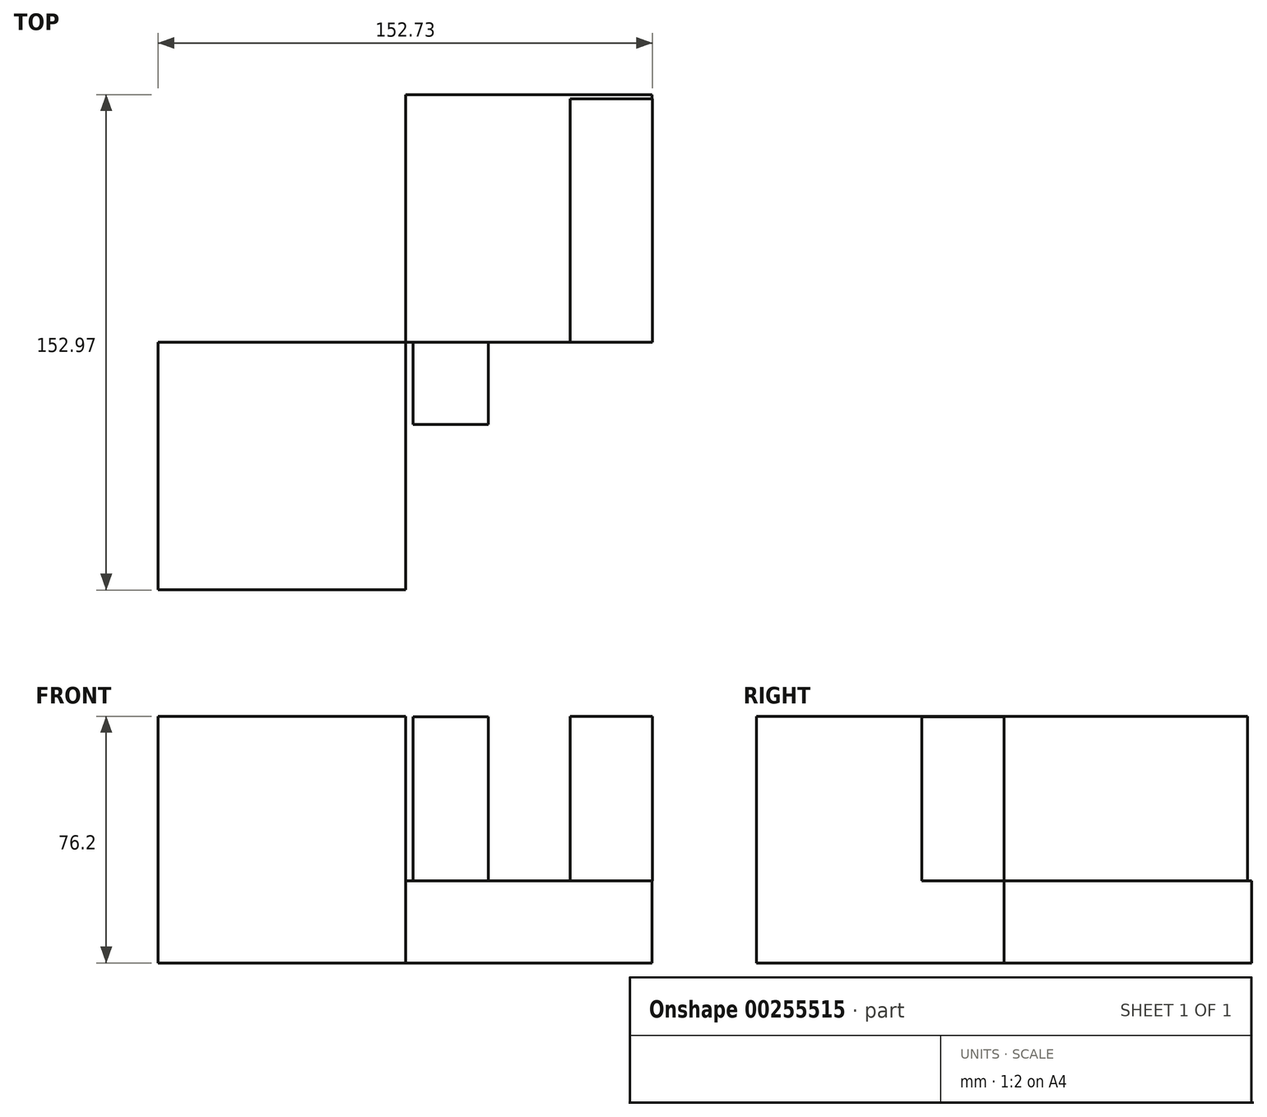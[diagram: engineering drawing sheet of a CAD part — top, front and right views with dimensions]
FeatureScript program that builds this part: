
annotation { "Feature Type Name" : "Feature", "Feature Type Description" : "" }
export const myFeature = defineFeature(function(context is Context, id is Id, definition is map)
    precondition{}
    {
        {
            var Q0;
            Q0=qCreatedBy(makeId("Top.planeOp"),FACE);
            var sketch = newSketch(context, id + "F0", { "sketchPlane" : qUnion([Q0])});
            skLineSegment(sketch, "E0.bottom", {"start": v(76, 76.48) * mm, "end": v(0, 76.48) * mm});
            skLineSegment(sketch, "E0.top", {"start": v(76, 0) * mm, "end": v(0, 0) * mm});
            skLineSegment(sketch, "E0.left", {"start": v(76, 76.48) * mm, "end": v(76, 0) * mm});
            skLineSegment(sketch, "E0.right", {"start": v(0, 76.48) * mm, "end": v(0, 0) * mm});
            skSolve(sketch);
        }
        {
            var Q0;
            Q0 = qSketchRegion(id + "F0", true);
            extrude(context, id + "F1", {"entities" : qUnion([Q0]), "depth" : 25.4 * mm});
        }
        {
            var Q0;
            Q0=qCreatedBy(makeId("Front.planeOp"),FACE);
            var sketch = newSketch(context, id + "F2", { "sketchPlane" : qUnion([Q0])});
            skLineSegment(sketch, "E1.bottom", {"start": v(2.7, 25.84) * mm, "end": v(76.24, 25.84) * mm});
            skLineSegment(sketch, "E1.top", {"start": v(2.7, 75.9) * mm, "end": v(76.24, 75.9) * mm});
            skLineSegment(sketch, "E1.left", {"start": v(2.7, 25.84) * mm, "end": v(2.7, 75.9) * mm});
            skLineSegment(sketch, "E1.right", {"start": v(76.24, 25.84) * mm, "end": v(76.24, 75.9) * mm});
            skSolve(sketch);
        }
        {
            var Q0;
            Q0 = qSketchRegion(id + "F2", true);
            extrude(context, id + "F3", {"entities" : qUnion([Q0]), "depth" : 25.4 * mm});
        }
        {
            var Q0;
            Q0=qCreatedBy(makeId("Right.planeOp"),FACE);
            var sketch = newSketch(context, id + "F4", { "sketchPlane" : qUnion([Q0])});
            skLineSegment(sketch, "E2.bottom", {"start": v(0, 76.17) * mm, "end": v(75.27, 76.17) * mm});
            skLineSegment(sketch, "E2.top", {"start": v(0, 25.38) * mm, "end": v(75.27, 25.38) * mm});
            skLineSegment(sketch, "E2.left", {"start": v(0, 76.17) * mm, "end": v(0, 25.38) * mm});
            skLineSegment(sketch, "E2.right", {"start": v(75.27, 76.17) * mm, "end": v(75.27, 25.38) * mm});
            skSolve(sketch);
        }
        {
            var Q0;
            Q0 = qSketchRegion(id + "F4", true);
            extrude(context, id + "F5", {"entities" : qUnion([Q0]), "depth" : 25.4 * mm});
        }
        {
            var Q0;
            Q0=makeQuery(id+"F5.opExtrude","CAP_FACE",FACE,{"disambiguationData":[OSD([sQuery(id+"F4.wireOp",EDGE,"E2.bottom"),sQuery(id+"F4.wireOp",EDGE,"E2.top"),sQuery(id+"F4.wireOp",EDGE,"E2.left"),sQuery(id+"F4.wireOp",EDGE,"E2.right")])],"isStart":false});
            var sketch = newSketch(context, id + "F6", { "sketchPlane" : qUnion([Q0])});
            skLineSegment(sketch, "E3.bottom", {"start": v(75.27, 76.17) * mm, "end": v(0, 76.17) * mm});
            skLineSegment(sketch, "E3.top", {"start": v(75.27, 25.38) * mm, "end": v(0, 25.38) * mm});
            skLineSegment(sketch, "E3.left", {"start": v(75.27, 76.17) * mm, "end": v(75.27, 25.38) * mm});
            skLineSegment(sketch, "E3.right", {"start": v(0, 76.17) * mm, "end": v(0, 25.38) * mm});
            skSolve(sketch);
        }
        {
            var Q0;
            Q0 = qSketchRegion(id + "F6", true);
            extrude(context, id + "F7", {"entities" : qUnion([Q0]), "depth" : 25.4 * mm});
        }
        {
            var Q0;
            Q0 = qSketchRegion(id + "F6", true);
            var Q1;
            Q1=makeQuery(id+"F7.opExtrude","CAP_FACE",FACE,{"disambiguationData":[OSD([sQuery(id+"F6.wireOp",EDGE,"E3.bottom"),sQuery(id+"F6.wireOp",EDGE,"E3.top"),sQuery(id+"F6.wireOp",EDGE,"E3.left"),sQuery(id+"F6.wireOp",EDGE,"E3.right")])],"isStart":false});
            extrude(context, id + "F8", {"entities" : qUnion([Q0, Q1]), "depth" : 25.4 * mm});
        }
        {
            var Q0;
            Q0=makeQuery(id+"F3.opExtrude","SWEPT_BODY",BODY,{"disambiguationData":[OSD([sQuery(id+"F2.wireOp",EDGE,"E1.bottom"),sQuery(id+"F2.wireOp",EDGE,"E1.top"),sQuery(id+"F2.wireOp",EDGE,"E1.left"),sQuery(id+"F2.wireOp",EDGE,"E1.right")])]});
            deleteBodies(context, id + "F9", {"entities" : qUnion([Q0])});
        }
        {
            var Q0;
            Q0=qCreatedBy(makeId("Top.planeOp"),FACE);
            var sketch = newSketch(context, id + "F10", { "sketchPlane" : qUnion([Q0])});
            skLineSegment(sketch, "E4.bottom", {"start": v(0, 0) * mm, "end": v(-76.53, 0) * mm});
            skLineSegment(sketch, "E4.top", {"start": v(0, -76.49) * mm, "end": v(-76.53, -76.49) * mm});
            skLineSegment(sketch, "E4.left", {"start": v(0, 0) * mm, "end": v(0, -76.49) * mm});
            skLineSegment(sketch, "E4.right", {"start": v(-76.53, 0) * mm, "end": v(-76.53, -76.49) * mm});
            skSolve(sketch);
        }
        {
            var Q0;
            Q0 = qSketchRegion(id + "F10", true);
            extrude(context, id + "F11", {"entities" : qUnion([Q0]), "depth" : 50.8 * mm});
        }
        {
            var Q0;
            Q0=qCreatedBy(makeId("Right.planeOp"),FACE);
            var sketch = newSketch(context, id + "F12", { "sketchPlane" : qUnion([Q0])});
            skLineSegment(sketch, "E5.bottom", {"start": v(0, 76.35) * mm, "end": v(-76.2, 76.35) * mm});
            skLineSegment(sketch, "E5.top", {"start": v(0, 50.85) * mm, "end": v(-76.2, 50.85) * mm});
            skLineSegment(sketch, "E5.left", {"start": v(0, 76.35) * mm, "end": v(0, 50.85) * mm});
            skLineSegment(sketch, "E5.right", {"start": v(-76.2, 76.35) * mm, "end": v(-76.2, 50.85) * mm});
            skSolve(sketch);
        }
        {
            var Q0;
            Q0 = qSketchRegion(id + "F12", true);
            extrude(context, id + "F13", {"entities" : qUnion([Q0]), "operationType" : NewBodyOperationType.ADD, "depth" : 25.4 * mm});
        }
        {
            var Q0;
            Q0=makeQuery(id+"F5.opExtrude","SWEPT_BODY",BODY,{"disambiguationData":[OSD([sQuery(id+"F4.wireOp",EDGE,"E2.bottom"),sQuery(id+"F4.wireOp",EDGE,"E2.top"),sQuery(id+"F4.wireOp",EDGE,"E2.left"),sQuery(id+"F4.wireOp",EDGE,"E2.right")])]});
            deleteBodies(context, id + "F14", {"entities" : qUnion([Q0])});
        }
        {
            var Q0;
            Q0=makeQuery(id+"F11.opExtrude","CAP_FACE",FACE,{"disambiguationData":[OSD([sQuery(id+"F10.wireOp",EDGE,"E4.bottom"),sQuery(id+"F10.wireOp",EDGE,"E4.top"),sQuery(id+"F10.wireOp",EDGE,"E4.left"),sQuery(id+"F10.wireOp",EDGE,"E4.right")])],"isStart":false});
            var sketch = newSketch(context, id + "F15", { "sketchPlane" : qUnion([Q0])});
            skLineSegment(sketch, "E6.bottom", {"start": v(0, 0) * mm, "end": v(-76.53, 0) * mm});
            skLineSegment(sketch, "E6.top", {"start": v(0, -76.49) * mm, "end": v(-76.53, -76.49) * mm});
            skLineSegment(sketch, "E6.left", {"start": v(0, 0) * mm, "end": v(0, -76.49) * mm});
            skLineSegment(sketch, "E6.right", {"start": v(-76.53, 0) * mm, "end": v(-76.53, -76.49) * mm});
            skSolve(sketch);
        }
        {
            var Q0;
            Q0=makeQuery(id+"F15.imprint","IMPRINT",FACE,{"disambiguationData":[TD([[makeQuery(id+"F15.imprint","IMPRINT",EDGE,{"derivedFrom":sQuery(id+"F15.wireOp",EDGE,"E6.bottom")}),1.0]])]});
            extrude(context, id + "F16", {"entities" : qUnion([Q0]), "operationType" : NewBodyOperationType.ADD, "depth" : 25.4 * mm});
        }
        {
            var Q0;
            Q0=qCreatedBy(makeId("Front.planeOp"),FACE);
            var sketch = newSketch(context, id + "F17", { "sketchPlane" : qUnion([Q0])});
            skLineSegment(sketch, "E7.bottom", {"start": v(2.19, 25.3) * mm, "end": v(25.5, 25.3) * mm});
            skLineSegment(sketch, "E7.top", {"start": v(2.19, 76.08) * mm, "end": v(25.5, 76.08) * mm});
            skLineSegment(sketch, "E7.left", {"start": v(2.19, 25.3) * mm, "end": v(2.19, 76.08) * mm});
            skLineSegment(sketch, "E7.right", {"start": v(25.5, 25.3) * mm, "end": v(25.5, 76.08) * mm});
            skSolve(sketch);
        }
        {
            var Q0;
            Q0=makeQuery(id+"F17.imprint","IMPRINT",FACE,{"disambiguationData":[TD([[makeQuery(id+"F17.imprint","IMPRINT",EDGE,{"derivedFrom":sQuery(id+"F17.wireOp",EDGE,"E7.bottom")}),1.0]])]});
            extrude(context, id + "F18", {"entities" : qUnion([Q0]), "depth" : 25.4 * mm});
        }
    });
